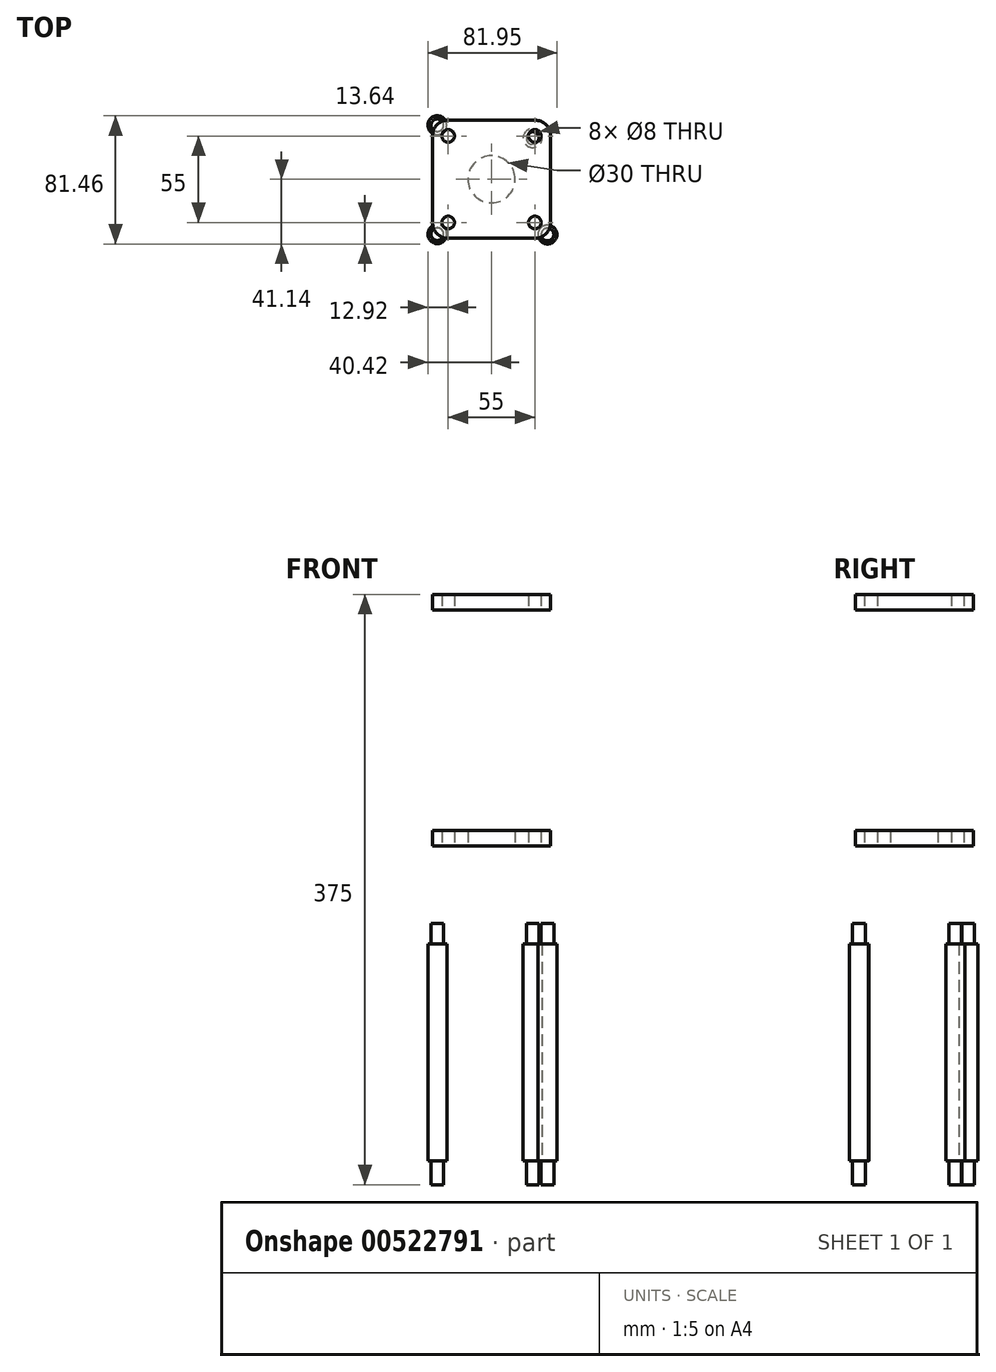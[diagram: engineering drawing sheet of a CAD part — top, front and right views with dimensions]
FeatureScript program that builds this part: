
annotation { "Feature Type Name" : "Feature", "Feature Type Description" : "" }
export const myFeature = defineFeature(function(context is Context, id is Id, definition is map)
    precondition{}
    {
        {
            var Q0;
            Q0=qCreatedBy(makeId("Top.planeOp"),FACE);
            var sketch = newSketch(context, id + "F0", { "sketchPlane" : qUnion([Q0])});
            skLineSegment(sketch, "E0.bottom", {"start": v(27.5, -37.5) * mm, "end": v(-27.5, -37.5) * mm});
            skLineSegment(sketch, "E0.top", {"start": v(27.5, 37.5) * mm, "end": v(-27.5, 37.5) * mm});
            skLineSegment(sketch, "E0.left", {"start": v(37.5, -27.5) * mm, "end": v(37.5, 27.5) * mm});
            skLineSegment(sketch, "E0.right", {"start": v(-37.5, -27.5) * mm, "end": v(-37.5, 27.5) * mm});
            skPoint(sketch, "E0.middle", {"position": v(0, 0) * mm});
            skPoint(sketch, "E1.visualSharp", {"position": v(-37.5, 37.5) * mm});
            skArc(sketch, "E1.filletArc", {"start": v(-27.5, 37.5) * mm, "mid": v(-34.57, 34.57) * mm, "end": v(-37.5, 27.5) * mm});
            skPoint(sketch, "E2.visualSharp", {"position": v(37.5, 37.5) * mm});
            skArc(sketch, "E2.filletArc", {"start": v(37.5, 27.5) * mm, "mid": v(34.57, 34.57) * mm, "end": v(27.5, 37.5) * mm});
            skPoint(sketch, "E3.visualSharp", {"position": v(37.5, -37.5) * mm});
            skArc(sketch, "E3.filletArc", {"start": v(27.5, -37.5) * mm, "mid": v(34.57, -34.57) * mm, "end": v(37.5, -27.5) * mm});
            skPoint(sketch, "E4.visualSharp", {"position": v(-37.5, -37.5) * mm});
            skArc(sketch, "E4.filletArc", {"start": v(-37.5, -27.5) * mm, "mid": v(-34.57, -34.57) * mm, "end": v(-27.5, -37.5) * mm});
            skCircle(sketch, "E5", {"center": v(27.5, 27.5) * mm, "radius": 4 * mm});
            skCircle(sketch, "E6", {"center": v(-27.5, 27.5) * mm, "radius": 4 * mm});
            skCircle(sketch, "E7", {"center": v(-27.5, -27.5) * mm, "radius": 4 * mm});
            skCircle(sketch, "E8", {"center": v(27.5, -27.5) * mm, "radius": 4 * mm});
            skCircle(sketch, "E9", {"center": v(0, 0) * mm, "radius": 15 * mm});
            skSolve(sketch);
        }
        {
            var Q0;
            Q0 = qSketchRegion(id + "F0", true);
            extrude(context, id + "F1", {"entities" : qUnion([Q0]), "depth" : 10 * mm, "offsetDistance" : 25 * mm});
        }
        {
            var Q0;
            Q0=qCreatedBy(makeId("Top.planeOp"),FACE);
            cPlane(context, id + "F2", {"entities" : qUnion([Q0]), "cplaneType" : CPlaneType.OFFSET, "offset" : 150 * mm, "width" : 150 * mm, "height" : 150 * mm});
        }
        {
            var Q0;
            Q0=qCreatedBy(id+"F2.planeOp",FACE);
            var sketch = newSketch(context, id + "F3", { "sketchPlane" : qUnion([Q0])});
            skLineSegment(sketch, "E10.bottom", {"start": v(-27.5, -37.5) * mm, "end": v(27.5, -37.5) * mm});
            skLineSegment(sketch, "E10.top", {"start": v(-27.5, 37.5) * mm, "end": v(27.5, 37.5) * mm});
            skLineSegment(sketch, "E10.left", {"start": v(-37.5, -27.5) * mm, "end": v(-37.5, 27.5) * mm});
            skLineSegment(sketch, "E10.right", {"start": v(37.5, -27.5) * mm, "end": v(37.5, 27.5) * mm});
            skPoint(sketch, "E10.middle", {"position": v(0, 0) * mm});
            skPoint(sketch, "E11.visualSharp", {"position": v(37.5, 37.5) * mm});
            skArc(sketch, "E11.filletArc", {"start": v(37.5, 27.5) * mm, "mid": v(34.57, 34.57) * mm, "end": v(27.5, 37.5) * mm});
            skPoint(sketch, "E12.visualSharp", {"position": v(-37.5, 37.5) * mm});
            skArc(sketch, "E12.filletArc", {"start": v(-27.5, 37.5) * mm, "mid": v(-34.57, 34.57) * mm, "end": v(-37.5, 27.5) * mm});
            skPoint(sketch, "E13.visualSharp", {"position": v(-37.5, -37.5) * mm});
            skArc(sketch, "E13.filletArc", {"start": v(-37.5, -27.5) * mm, "mid": v(-34.57, -34.57) * mm, "end": v(-27.5, -37.5) * mm});
            skPoint(sketch, "E14.visualSharp", {"position": v(37.5, -37.5) * mm});
            skArc(sketch, "E14.filletArc", {"start": v(27.5, -37.5) * mm, "mid": v(34.57, -34.57) * mm, "end": v(37.5, -27.5) * mm});
            skCircle(sketch, "E15", {"center": v(-27.5, 27.5) * mm, "radius": 4 * mm});
            skCircle(sketch, "E16", {"center": v(27.5, 27.5) * mm, "radius": 4 * mm});
            skCircle(sketch, "E17", {"center": v(27.5, -27.5) * mm, "radius": 4 * mm});
            skCircle(sketch, "E18", {"center": v(-27.5, -27.5) * mm, "radius": 4 * mm});
            skSolve(sketch);
        }
        {
            var Q0;
            Q0 = qSketchRegion(id + "F3", true);
            extrude(context, id + "F4", {"entities" : qUnion([Q0]), "depth" : 10 * mm, "offsetDistance" : 25 * mm});
        }
        {
            var Q0;
            Q0=qCreatedBy(makeId("Top.planeOp"),FACE);
            cPlane(context, id + "F5", {"entities" : qUnion([Q0]), "cplaneType" : CPlaneType.OFFSET, "offset" : 200 * mm, "oppositeDirection" : true, "width" : 150 * mm, "height" : 150 * mm});
        }
        {
            var Q0;
            Q0=qCreatedBy(id+"F5.planeOp",FACE);
            var sketch = newSketch(context, id + "F6", { "sketchPlane" : qUnion([Q0])});
            skCircle(sketch, "E19", {"center": v(35.53, -35.14) * mm, "radius": 6 * mm});
            skCircle(sketch, "E20", {"center": v(26.06, 26.1) * mm, "radius": 6 * mm});
            skCircle(sketch, "E21", {"center": v(-34.42, 34.32) * mm, "radius": 6 * mm});
            skCircle(sketch, "E22", {"center": v(-34.42, -34.9) * mm, "radius": 6 * mm});
            skSolve(sketch);
        }
        {
            var Q0;
            Q0 = qSketchRegion(id + "F6", true);
            extrude(context, id + "F7", {"entities" : qUnion([Q0]), "depth" : 138 * mm, "offsetDistance" : 25 * mm});
        }
        {
            var Q0;
            Q0=makeQuery(id+"F7.opExtrude","CAP_FACE",FACE,{"disambiguationData":[OSD([sQuery(id+"F6.wireOp",EDGE,"E19")])],"isStart":true});
            var sketch = newSketch(context, id + "F8", { "sketchPlane" : qUnion([Q0])});
            skCircle(sketch, "E23", {"center": v(35.53, 35.14) * mm, "radius": 4 * mm});
            skSolve(sketch);
        }
        {
            var Q0;
            Q0 = qSketchRegion(id + "F8", true);
            extrude(context, id + "F9", {"entities" : qUnion([Q0]), "operationType" : NewBodyOperationType.ADD, "depth" : 15 * mm, "offsetDistance" : 25 * mm});
        }
        {
            var Q0;
            Q0=makeQuery(id+"F7.opExtrude","CAP_FACE",FACE,{"disambiguationData":[OSD([sQuery(id+"F6.wireOp",EDGE,"E20")])],"isStart":true});
            var sketch = newSketch(context, id + "F10", { "sketchPlane" : qUnion([Q0])});
            skCircle(sketch, "E24", {"center": v(26.06, -26.1) * mm, "radius": 4 * mm});
            skSolve(sketch);
        }
        {
            var Q0;
            Q0 = qSketchRegion(id + "F10", true);
            extrude(context, id + "F11", {"entities" : qUnion([Q0]), "operationType" : NewBodyOperationType.ADD, "depth" : 15 * mm, "offsetDistance" : 25 * mm});
        }
        {
            var Q0;
            Q0=makeQuery(id+"F7.opExtrude","CAP_FACE",FACE,{"disambiguationData":[OSD([sQuery(id+"F6.wireOp",EDGE,"E22")])],"isStart":true});
            var sketch = newSketch(context, id + "F12", { "sketchPlane" : qUnion([Q0])});
            skCircle(sketch, "E25", {"center": v(-34.42, 34.9) * mm, "radius": 4 * mm});
            skSolve(sketch);
        }
        {
            var Q0;
            Q0 = qSketchRegion(id + "F12", true);
            extrude(context, id + "F13", {"entities" : qUnion([Q0]), "operationType" : NewBodyOperationType.ADD, "depth" : 15 * mm, "offsetDistance" : 25 * mm});
        }
        {
            var Q0;
            Q0=makeQuery(id+"F7.opExtrude","CAP_FACE",FACE,{"disambiguationData":[OSD([sQuery(id+"F6.wireOp",EDGE,"E21")])],"isStart":true});
            var sketch = newSketch(context, id + "F14", { "sketchPlane" : qUnion([Q0])});
            skCircle(sketch, "E26", {"center": v(-34.42, -34.32) * mm, "radius": 4 * mm});
            skSolve(sketch);
        }
        {
            var Q0;
            Q0 = qSketchRegion(id + "F14", true);
            extrude(context, id + "F15", {"entities" : qUnion([Q0]), "operationType" : NewBodyOperationType.ADD, "depth" : 15 * mm, "offsetDistance" : 25 * mm});
        }
        {
            var Q0;
            Q0=makeQuery(id+"F7.opExtrude","CAP_FACE",FACE,{"disambiguationData":[OSD([sQuery(id+"F6.wireOp",EDGE,"E20")])],"isStart":false});
            var sketch = newSketch(context, id + "F16", { "sketchPlane" : qUnion([Q0])});
            skCircle(sketch, "E27", {"center": v(26.06, 26.1) * mm, "radius": 4 * mm});
            skSolve(sketch);
        }
        {
            var Q0;
            Q0 = qSketchRegion(id + "F16", true);
            extrude(context, id + "F17", {"entities" : qUnion([Q0]), "operationType" : NewBodyOperationType.ADD, "depth" : 13 * mm, "offsetDistance" : 25 * mm});
        }
        {
            var Q0;
            Q0=makeQuery(id+"F7.opExtrude","CAP_FACE",FACE,{"disambiguationData":[OSD([sQuery(id+"F6.wireOp",EDGE,"E19")])],"isStart":false});
            var sketch = newSketch(context, id + "F18", { "sketchPlane" : qUnion([Q0])});
            skCircle(sketch, "E28", {"center": v(35.53, -35.14) * mm, "radius": 4 * mm});
            skSolve(sketch);
        }
        {
            var Q0;
            Q0 = qSketchRegion(id + "F18", true);
            extrude(context, id + "F19", {"entities" : qUnion([Q0]), "operationType" : NewBodyOperationType.ADD, "depth" : 13 * mm, "offsetDistance" : 25 * mm});
        }
        {
            var Q0;
            Q0=makeQuery(id+"F7.opExtrude","CAP_FACE",FACE,{"disambiguationData":[OSD([sQuery(id+"F6.wireOp",EDGE,"E22")])],"isStart":false});
            var sketch = newSketch(context, id + "F20", { "sketchPlane" : qUnion([Q0])});
            skCircle(sketch, "E29", {"center": v(-34.42, -34.9) * mm, "radius": 4 * mm});
            skSolve(sketch);
        }
        {
            var Q0;
            Q0 = qSketchRegion(id + "F20", true);
            extrude(context, id + "F21", {"entities" : qUnion([Q0]), "operationType" : NewBodyOperationType.ADD, "depth" : 13 * mm, "offsetDistance" : 25 * mm});
        }
        {
            var Q0;
            Q0=makeQuery(id+"F7.opExtrude","CAP_FACE",FACE,{"disambiguationData":[OSD([sQuery(id+"F6.wireOp",EDGE,"E21")])],"isStart":false});
            var sketch = newSketch(context, id + "F22", { "sketchPlane" : qUnion([Q0])});
            skCircle(sketch, "E30", {"center": v(-34.42, 34.32) * mm, "radius": 4 * mm});
            skSolve(sketch);
        }
        {
            var Q0;
            Q0 = qSketchRegion(id + "F22", true);
            extrude(context, id + "F23", {"entities" : qUnion([Q0]), "operationType" : NewBodyOperationType.ADD, "depth" : 13 * mm, "offsetDistance" : 25 * mm});
        }
    });
